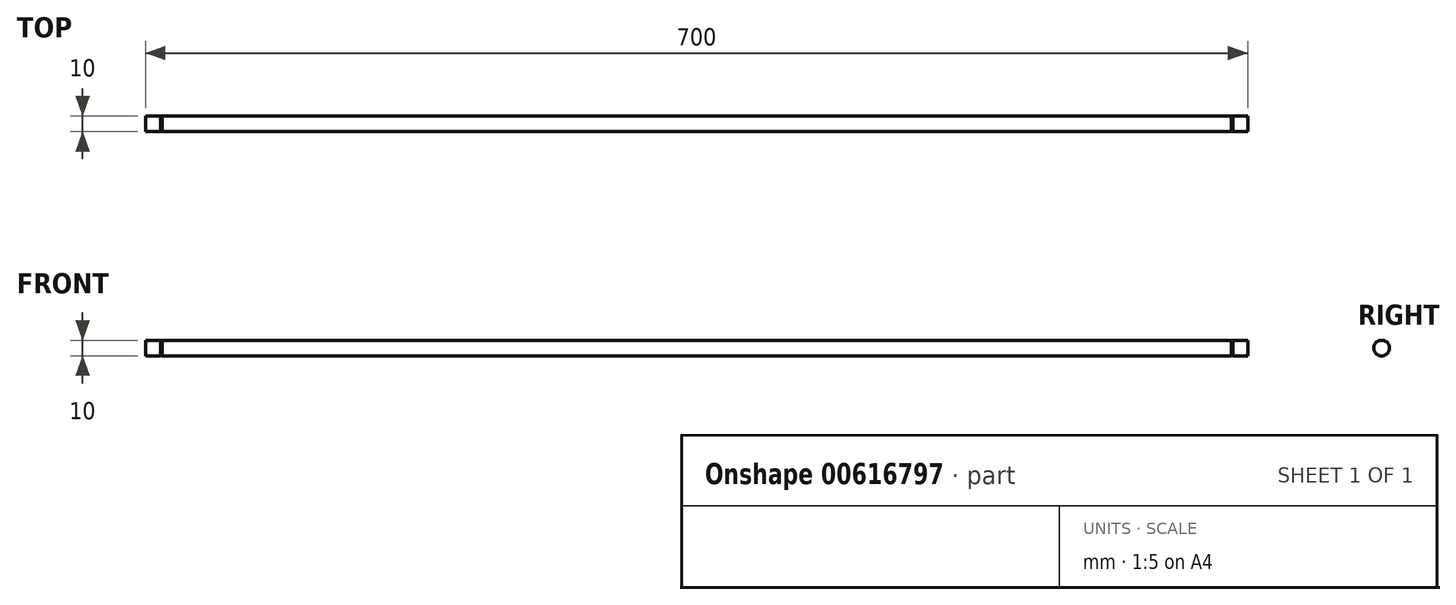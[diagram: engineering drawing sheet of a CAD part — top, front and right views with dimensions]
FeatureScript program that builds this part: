
annotation { "Feature Type Name" : "Feature", "Feature Type Description" : "" }
export const myFeature = defineFeature(function(context is Context, id is Id, definition is map)
    precondition{}
    {
        {
            var Q0;
            Q0=qCreatedBy(makeId("Right.planeOp"),FACE);
            var sketch = newSketch(context, id + "F0", { "sketchPlane" : qUnion([Q0])});
            skCircle(sketch, "E0", {"center": v(0, 0) * mm, "radius": 5 * mm});
            skSolve(sketch);
        }
        {
            var Q0;
            Q0=makeQuery(id+"F0.imprint","IMPRINT",FACE,{"disambiguationData":[TD([[makeQuery(id+"F0.imprint","IMPRINT",EDGE,{"derivedFrom":sQuery(id+"F0.wireOp",EDGE,"E0")}),1.0]])]});
            extrude(context, id + "F1", {"entities" : qUnion([Q0]), "depth" : 700 * mm, "offsetDistance" : 25 * mm, "hasSecondDirection" : true, "secondDirectionOppositeDirection" : true, "secondDirectionDepth" : (1037 / 2) * mm, "symmetric" : true});
        }
        {
            var Q0;
            Q0=qCreatedBy(makeId("Front.planeOp"),FACE);
            var sketch = newSketch(context, id + "F2", { "sketchPlane" : qUnion([Q0])});
            skLineSegment(sketch, "E1", {"start": v(0, 0) * mm, "end": v(372.6, 0) * mm, "construction": true});
            skLineSegment(sketch, "E2", {"start": v(339.5, 5.8) * mm, "end": v(339.5, 4.8) * mm});
            skLineSegment(sketch, "E3", {"start": v(339.5, 4.8) * mm, "end": v(340.6, 4.8) * mm});
            skLineSegment(sketch, "E4", {"start": v(340.6, 4.8) * mm, "end": v(340.6, 5.8) * mm});
            skLineSegment(sketch, "E5", {"start": v(340.6, 5.8) * mm, "end": v(339.5, 5.8) * mm});
            skLineSegment(sketch, "E6.bottom", {"start": v(-339.5, 4.8) * mm, "end": v(-340.6, 4.8) * mm});
            skLineSegment(sketch, "E6.top", {"start": v(-339.5, 5.8) * mm, "end": v(-340.6, 5.8) * mm});
            skLineSegment(sketch, "E6.left", {"start": v(-339.5, 4.8) * mm, "end": v(-339.5, 5.8) * mm});
            skLineSegment(sketch, "E6.right", {"start": v(-340.6, 4.8) * mm, "end": v(-340.6, 5.8) * mm});
            skSolve(sketch);
        }
        {
            var Q0;
            Q0 = qSketchRegion(id + "F2", true);
            var Q1;
            Q1=sQuery(id+"F2.wireOp",EDGE,"E1");
            revolve(context, id + "F3", {"operationType" : NewBodyOperationType.REMOVE, "surfaceOperationType" : NewSurfaceOperationType.NEW, "entities" : qUnion([Q0]), "axis" : qUnion([Q1]), "revolveType" : RevolveType.FULL, "oppositeDirection" : true});
        }
    });
